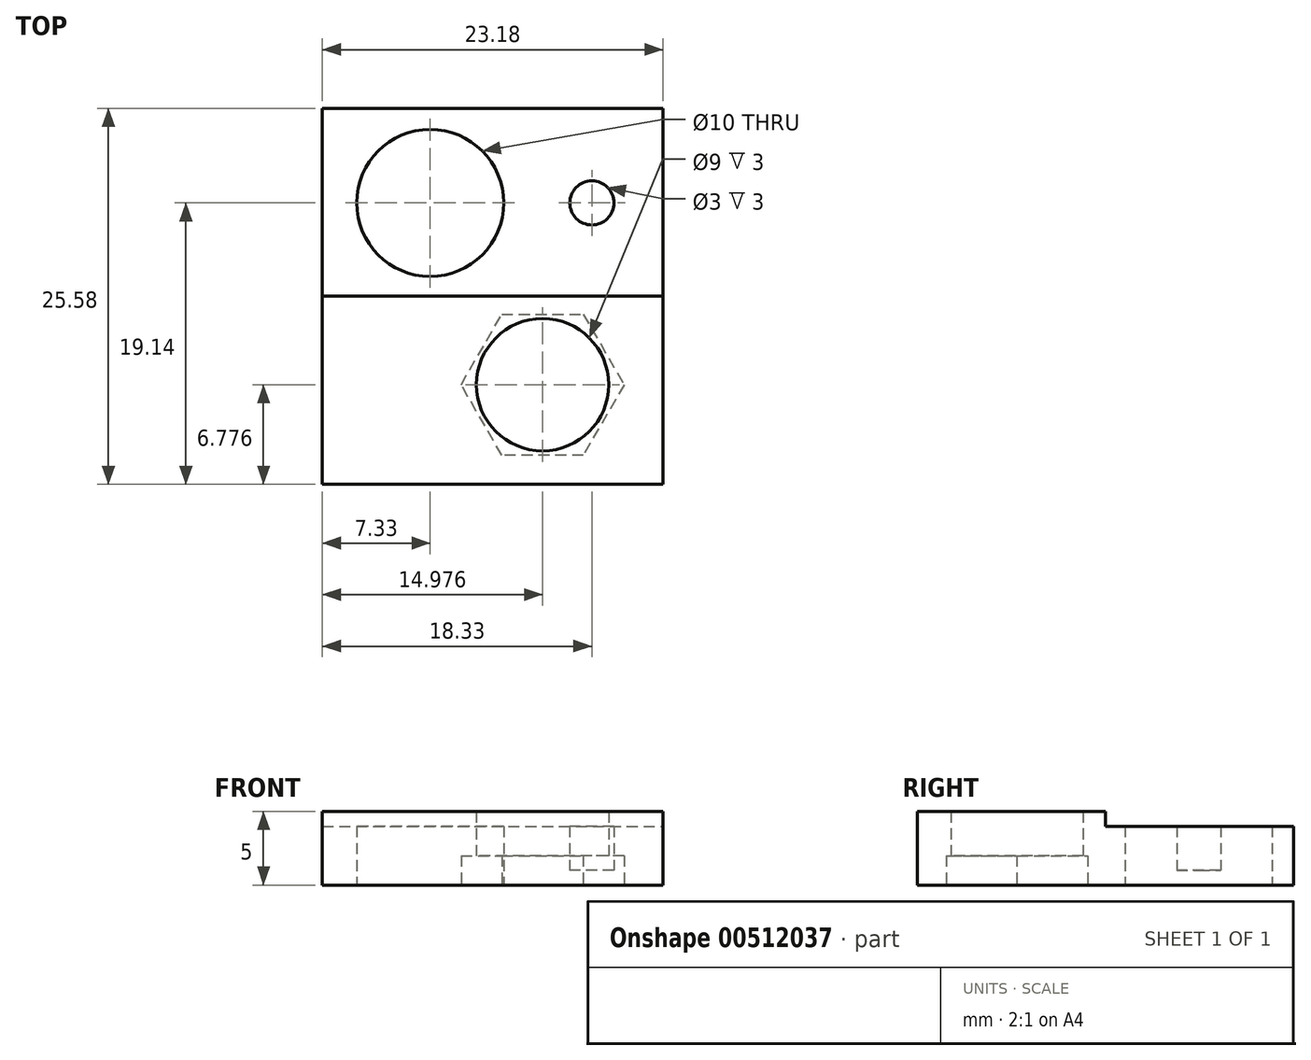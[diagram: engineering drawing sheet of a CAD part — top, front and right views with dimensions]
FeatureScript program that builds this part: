
annotation { "Feature Type Name" : "Feature", "Feature Type Description" : "" }
export const myFeature = defineFeature(function(context is Context, id is Id, definition is map)
    precondition{}
    {
        {
            var Q0;
            Q0=qCreatedBy(makeId("Top.planeOp"),FACE);
            var sketch = newSketch(context, id + "F0", { "sketchPlane" : qUnion([Q0])});
            skCircle(sketch, "E0", {"center": v(0, 0) * mm, "radius": 5 * mm});
            skCircle(sketch, "E1", {"center": v(11, 0) * mm, "radius": 1.5 * mm});
            skLineSegment(sketch, "E2.bottom", {"start": v(-7.33, 6.44) * mm, "end": v(15.85, 6.44) * mm});
            skLineSegment(sketch, "E2.top", {"start": v(-7.33, -19.14) * mm, "end": v(15.85, -19.14) * mm});
            skLineSegment(sketch, "E2.left", {"start": v(-7.33, 6.44) * mm, "end": v(-7.33, -19.14) * mm});
            skLineSegment(sketch, "E2.right", {"start": v(15.85, 6.44) * mm, "end": v(15.85, -19.14) * mm});
            skCircle(sketch, "E3", {"center": v(7.65, -12.36) * mm, "radius": 4.5 * mm});
            skLineSegment(sketch, "E4", {"start": v(4.87, -7.56) * mm, "end": v(10.42, -7.56) * mm});
            skLineSegment(sketch, "E5", {"start": v(10.42, -7.56) * mm, "end": v(13.19, -12.36) * mm});
            skLineSegment(sketch, "E6", {"start": v(13.19, -12.36) * mm, "end": v(10.42, -17.16) * mm});
            skLineSegment(sketch, "E7", {"start": v(10.42, -17.16) * mm, "end": v(4.87, -17.16) * mm});
            skLineSegment(sketch, "E8", {"start": v(4.87, -17.16) * mm, "end": v(2.1, -12.36) * mm});
            skLineSegment(sketch, "E9", {"start": v(2.1, -12.36) * mm, "end": v(4.87, -7.56) * mm});
            skLineSegment(sketch, "E10", {"start": v(4.87, -17.16) * mm, "end": v(7.65, -12.36) * mm, "construction": true});
            skLineSegment(sketch, "E11", {"start": v(2.1, -12.36) * mm, "end": v(7.65, -12.36) * mm, "construction": true});
            skSolve(sketch);
        }
        {
            var Q0;
            Q0=makeQuery(id+"F0.imprint","IMPRINT",FACE,{"disambiguationData":[TD([[makeQuery(id+"F0.imprint","IMPRINT",EDGE,{"derivedFrom":sQuery(id+"F0.wireOp",EDGE,"E3")}),-1.0]])]});
            var Q1;
            Q1=makeQuery(id+"F0.imprint","IMPRINT",FACE,{"disambiguationData":[TD([[makeQuery(id+"F0.imprint","IMPRINT",EDGE,{"derivedFrom":sQuery(id+"F0.wireOp",EDGE,"E0")}),-1.0]])]});
            var Q2;
            Q2=makeQuery(id+"F0.imprint","IMPRINT",FACE,{"disambiguationData":[TD([[makeQuery(id+"F0.imprint","IMPRINT",EDGE,{"derivedFrom":sQuery(id+"F0.wireOp",EDGE,"E1")}),1.0]])]});
            extrude(context, id + "F1", {"entities" : qUnion([Q0, Q1, Q2]), "depth" : 5 * mm, "offsetDistance" : 25 * mm});
        }
        {
            var Q0;
            Q0=makeQuery(id+"F0.imprint","IMPRINT",FACE,{"disambiguationData":[TD([[makeQuery(id+"F0.imprint","IMPRINT",EDGE,{"derivedFrom":sQuery(id+"F0.wireOp",EDGE,"E3")}),-1.0]])]});
            extrude(context, id + "F2", {"entities" : qUnion([Q0]), "operationType" : NewBodyOperationType.REMOVE, "depth" : 2 * mm, "offsetDistance" : 25 * mm});
        }
        {
            var Q0;
            Q0=makeQuery(id+"F0.imprint","IMPRINT",FACE,{"disambiguationData":[TD([[makeQuery(id+"F0.imprint","IMPRINT",EDGE,{"derivedFrom":sQuery(id+"F0.wireOp",EDGE,"E1")}),1.0]])]});
            extrude(context, id + "F3", {"entities" : qUnion([Q0]), "operationType" : NewBodyOperationType.REMOVE, "endBound" : BoundingType.UP_TO_NEXT, "depth" : 3 * mm, "offsetDistance" : 25 * mm, "hasSecondDirection" : true, "secondDirectionOppositeDirection" : true, "secondDirectionDepth" : -1 * mm});
        }
        {
            var Q0;
            Q0=makeQuery(id+"F1.opExtrude","CAP_FACE",FACE,{"disambiguationData":[OSD([sQuery(id+"F0.wireOp",EDGE,"E0"),sQuery(id+"F0.wireOp",EDGE,"E2.bottom"),sQuery(id+"F0.wireOp",EDGE,"E2.top"),sQuery(id+"F0.wireOp",EDGE,"E2.left"),sQuery(id+"F0.wireOp",EDGE,"E2.right"),sQuery(id+"F0.wireOp",EDGE,"E3")])],"isStart":false});
            var sketch = newSketch(context, id + "F4", { "sketchPlane" : qUnion([Q0])});
            skLineSegment(sketch, "E12.bottom", {"start": v(-7.33, -6.35) * mm, "end": v(15.85, -6.35) * mm});
            skLineSegment(sketch, "E12.top", {"start": v(-7.33, 6.44) * mm, "end": v(15.85, 6.44) * mm});
            skLineSegment(sketch, "E12.left", {"start": v(-7.33, -6.35) * mm, "end": v(-7.33, 6.44) * mm});
            skLineSegment(sketch, "E12.right", {"start": v(15.85, -6.35) * mm, "end": v(15.85, 6.44) * mm});
            skSolve(sketch);
        }
        {
            var Q0;
            Q0 = qSketchRegion(id + "F4", true);
            var Q1;
            Q1=makeQuery(id+"F4.imprint","IMPRINT",FACE,{"disambiguationData":[TD([[makeQuery(id+"F4.imprint","IMPRINT",EDGE,{"derivedFrom":sQuery(id+"F4.wireOp",EDGE,"E12.top")}),-1.0]])]});
            extrude(context, id + "F5", {"entities" : qUnion([Q0, Q1]), "operationType" : NewBodyOperationType.REMOVE, "oppositeDirection" : true, "depth" : 1 * mm, "offsetDistance" : 25 * mm});
        }
    });
